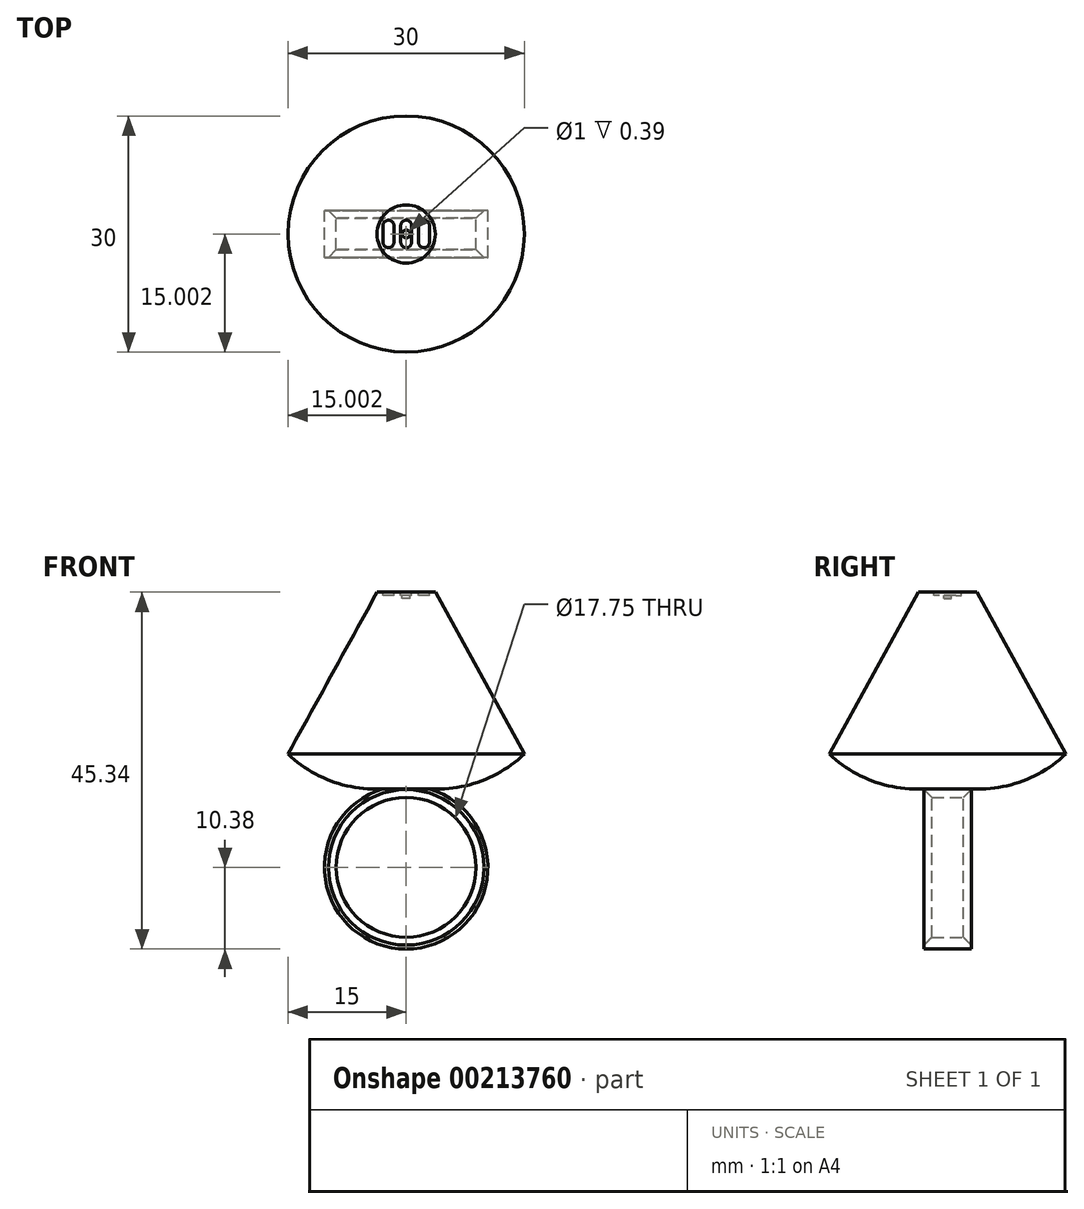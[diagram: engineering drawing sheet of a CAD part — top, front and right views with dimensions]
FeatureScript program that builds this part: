
annotation { "Feature Type Name" : "Feature", "Feature Type Description" : "" }
export const myFeature = defineFeature(function(context is Context, id is Id, definition is map)
    precondition{}
    {
        {
            var Q0;
            Q0=qCreatedBy(makeId("Front.planeOp"),FACE);
            var sketch = newSketch(context, id + "F0", { "sketchPlane" : qUnion([Q0])});
            skCircle(sketch, "E0", {"center": v(0, 0) * mm, "radius": 8.88 * mm});
            skCircle(sketch, "E1.0", {"center": v(0, 0) * mm, "radius": 10.38 * mm});
            skLineSegment(sketch, "E2", {"start": v(0, 9.96) * mm, "end": v(2.9, 9.96) * mm});
            skArc(sketch, "E3", {"start": v(2.9, 9.96) * mm, "mid": v(9.4, 10.93) * mm, "end": v(15, 14.38) * mm});
            skLineSegment(sketch, "E4", {"start": v(15, 14.38) * mm, "end": v(3.7, 34.96) * mm});
            skLineSegment(sketch, "E5", {"start": v(3.7, 34.96) * mm, "end": v(0, 34.96) * mm});
            skPoint(sketch, "E6", {"position": v(0, 9.96) * mm});
            skPoint(sketch, "E7.orphan", {"position": v(-2.9, 9.96) * mm});
            skLineSegment(sketch, "E8", {"start": v(0, 34.96) * mm, "end": v(0, 9.96) * mm});
            skSolve(sketch);
        }
        {
            var Q0;
            Q0=qCreatedBy(makeId("Top.planeOp"),FACE);
            var sketch = newSketch(context, id + "F1", { "sketchPlane" : qUnion([Q0])});
            skCircle(sketch, "E9", {"center": v(0, 0) * mm, "radius": 4.62 * mm});
            skSolve(sketch);
        }
        {
            var Q0;
            {var subQ1=sQuery(id+"F0.wireOp",EDGE,"E3");Q0=makeQuery(id+"F0.imprint","IMPRINT",FACE,{"disambiguationData":[TD([[makeQuery(id+"F0.imprint","IMPRINT",EDGE,{"derivedFrom":subQ1}),1.0]])]});}
            var Q1;
            Q1=sQuery(id+"F1.wireOp",EDGE,"E9");
            revolve(context, id + "F2", {"entities" : qUnion([Q0]), "axis" : qUnion([Q1]), "revolveType" : RevolveType.FULL});
        }
        {
            var Q0;
            Q0=makeQuery(id+"F0.imprint","IMPRINT",FACE,{"disambiguationData":[TD([[makeQuery(id+"F0.imprint","IMPRINT",EDGE,{"derivedFrom":sQuery(id+"F0.wireOp",EDGE,"E0")}),-1.0]])]});
            var Q1;
            {var subQ0=sQuery(id+"F0.wireOp",EDGE,"E2");Q1=makeQuery(id+"F0.imprint","IMPRINT",FACE,{"disambiguationData":[TD([[makeQuery(id+"F0.imprint","IMPRINT",EDGE,{"derivedFrom":subQ0}),1.0]])]});}
            extrude(context, id + "F3", {"entities" : qUnion([Q0, Q1]), "operationType" : NewBodyOperationType.ADD, "depth" : 3 * mm, "hasSecondDirection" : true, "secondDirectionOppositeDirection" : true, "secondDirectionDepth" : 3 * mm});
        }
        {
            var Q0;
            Q0=makeQuery(id+"F3.opExtrude","CAP_EDGE",EDGE,{"disambiguationData":[OSD([sQuery(id+"F0.wireOp",EDGE,"E0")])],"isStart":false});
            var Q1;
            Q1=makeQuery(id+"F3.opExtrude","CAP_EDGE",EDGE,{"disambiguationData":[OSD([sQuery(id+"F0.wireOp",EDGE,"E0")])],"isStart":true});
            chamfer(context, id + "F4", {"entities" : qUnion([Q0, Q1]), "width" : 1 * mm, "tangentPropagation" : true});
        }
        {
            var Q0;
            Q0=makeQuery(id+"F2.opRevolve","SWEPT_FACE",FACE,{"disambiguationData":[OSD([sQuery(id+"F0.wireOp",EDGE,"E5")])]});
            var sketch = newSketch(context, id + "F5", { "sketchPlane" : qUnion([Q0])});
            skLineSegment(sketch, "E10.bottom", {"start": v(-0.7, 1.05) * mm, "end": v(-0.7, -1.04) * mm});
            skArc(sketch, "E11.filletArc", {"start": v(0.7, 1.05) * mm, "mid": v(0.5, 1.55) * mm, "end": v(0, 1.75) * mm});
            skArc(sketch, "E12.filletArc", {"start": v(0, 1.75) * mm, "mid": v(-0.5, 1.55) * mm, "end": v(-0.7, 1.05) * mm});
            skArc(sketch, "E13.filletArc", {"start": v(0, -1.74) * mm, "mid": v(0.5, -1.53) * mm, "end": v(0.7, -1.04) * mm});
            skArc(sketch, "E14.filletArc", {"start": v(-0.7, -1.04) * mm, "mid": v(-0.5, -1.53) * mm, "end": v(0, -1.74) * mm});
            skLineSegment(sketch, "E15.bottom", {"start": v(-2.95, 1.05) * mm, "end": v(-2.95, -1.04) * mm});
            skLineSegment(sketch, "E15.top", {"start": v(-1.55, 1.05) * mm, "end": v(-1.55, -1.04) * mm});
            skArc(sketch, "E16.filletArc", {"start": v(-1.55, 1.05) * mm, "mid": v(-1.75, 1.55) * mm, "end": v(-2.25, 1.75) * mm});
            skArc(sketch, "E17.filletArc", {"start": v(-2.25, 1.75) * mm, "mid": v(-2.74, 1.55) * mm, "end": v(-2.95, 1.05) * mm});
            skArc(sketch, "E18.filletArc", {"start": v(-2.25, -1.74) * mm, "mid": v(-1.75, -1.53) * mm, "end": v(-1.55, -1.04) * mm});
            skArc(sketch, "E19.filletArc", {"start": v(-2.95, -1.04) * mm, "mid": v(-2.74, -1.53) * mm, "end": v(-2.25, -1.74) * mm});
            skLineSegment(sketch, "E20", {"start": v(0.7, 1.05) * mm, "end": v(0.7, -1.04) * mm});
            skCircle(sketch, "E21", {"center": v(0, 0) * mm, "radius": 0.5 * mm});
            skLineSegment(sketch, "E22.bottom", {"start": v(1.56, 1.05) * mm, "end": v(1.56, -1.04) * mm});
            skLineSegment(sketch, "E22.top", {"start": v(2.96, 1.05) * mm, "end": v(2.96, -1.04) * mm});
            skArc(sketch, "E23.filletArc", {"start": v(2.96, 1.05) * mm, "mid": v(2.75, 1.55) * mm, "end": v(2.26, 1.75) * mm});
            skArc(sketch, "E24.filletArc", {"start": v(2.26, 1.75) * mm, "mid": v(1.76, 1.55) * mm, "end": v(1.56, 1.05) * mm});
            skArc(sketch, "E25.filletArc", {"start": v(2.26, -1.74) * mm, "mid": v(2.75, -1.53) * mm, "end": v(2.96, -1.04) * mm});
            skArc(sketch, "E26.filletArc", {"start": v(1.56, -1.04) * mm, "mid": v(1.76, -1.53) * mm, "end": v(2.26, -1.74) * mm});
            skSolve(sketch);
        }
        {
            var Q0;
            Q0=makeQuery(id+"F5.imprint","IMPRINT",FACE,{"disambiguationData":[TD([[makeQuery(id+"F5.imprint","IMPRINT",EDGE,{"derivedFrom":sQuery(id+"F5.wireOp",EDGE,"E10.bottom")}),1.0]])]});
            var Q1;
            Q1=makeQuery(id+"F5.imprint","IMPRINT",FACE,{"disambiguationData":[TD([[makeQuery(id+"F5.imprint","IMPRINT",EDGE,{"derivedFrom":sQuery(id+"F5.wireOp",EDGE,"E15.bottom")}),1.0]])]});
            var Q2;
            Q2=makeQuery(id+"F5.imprint","IMPRINT",FACE,{"disambiguationData":[TD([[makeQuery(id+"F5.imprint","IMPRINT",EDGE,{"derivedFrom":sQuery(id+"F5.wireOp",EDGE,"E22.bottom")}),1.0]])]});
            extrude(context, id + "F6", {"entities" : qUnion([Q0, Q1, Q2]), "operationType" : NewBodyOperationType.REMOVE, "oppositeDirection" : true, "depth" : .43 * mm, "offsetDistance" : 25 * mm});
        }
        {
            var Q0;
            Q0=makeQuery(id+"F6.boolean.opBoolean","SPLIT",FACE,{"disambiguationData":[TD([makeQuery(id+"F6.opExtrude","SWEPT_FACE",FACE,{"disambiguationData":[OSD([sQuery(id+"F5.wireOp",EDGE,"E21")])]})])],"derivedFrom":makeQuery(id+"F2.opRevolve","SWEPT_FACE",FACE,{"disambiguationData":[OSD([sQuery(id+"F0.wireOp",EDGE,"E5")])]})});
            extrude(context, id + "F7", {"entities" : qUnion([Q0]), "operationType" : NewBodyOperationType.REMOVE, "oppositeDirection" : true, "depth" : .82 * mm, "offsetDistance" : 25 * mm});
        }
    });
